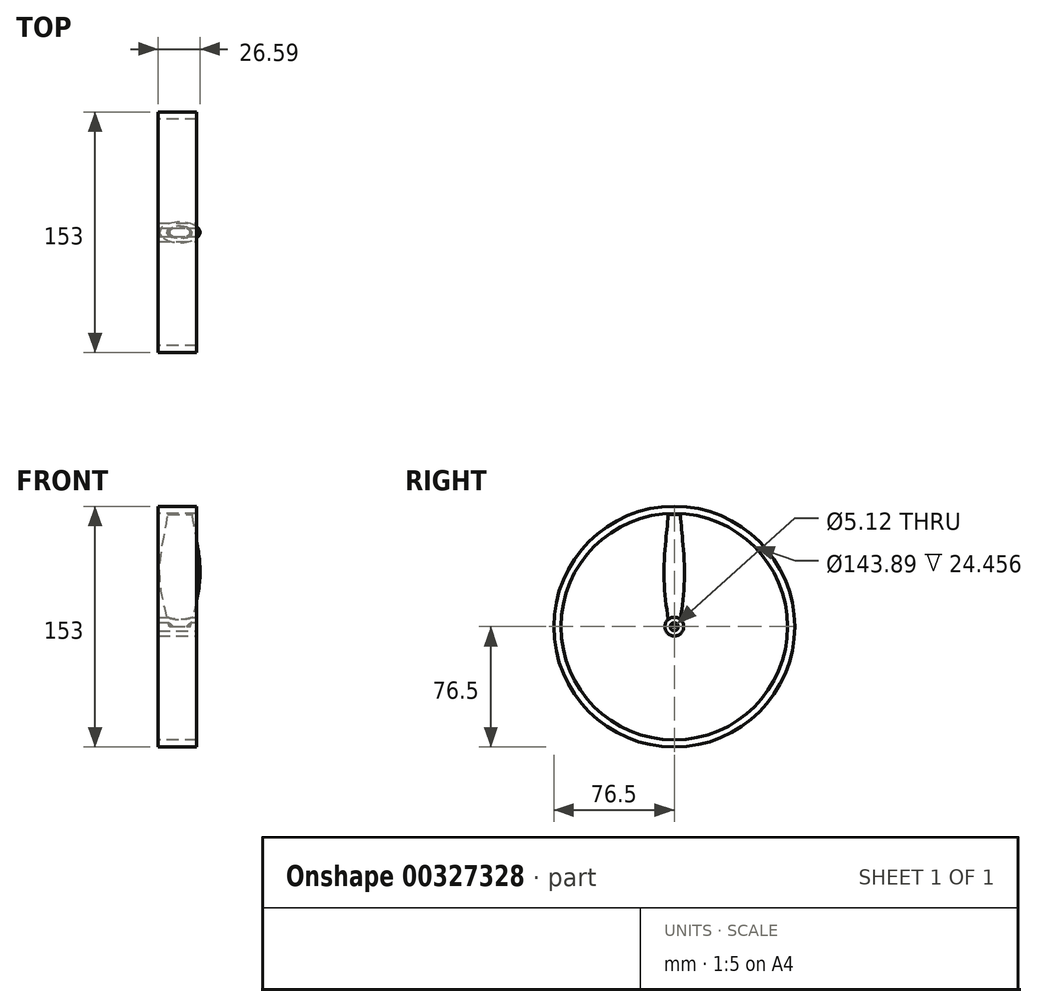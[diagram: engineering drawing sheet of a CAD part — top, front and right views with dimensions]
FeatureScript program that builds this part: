
annotation { "Feature Type Name" : "Feature", "Feature Type Description" : "" }
export const myFeature = defineFeature(function(context is Context, id is Id, definition is map)
    precondition{}
    {
        {
            var Q0;
            Q0=qCreatedBy(makeId("Front.planeOp"),FACE);
            var sketch = newSketch(context, id + "F0", { "sketchPlane" : qUnion([Q0])});
            skLineSegment(sketch, "E0.bottom", {"start": v(-13.8, -76.5) * mm, "end": v(10.66, -76.5) * mm});
            skLineSegment(sketch, "E0.top", {"start": v(-13.8, -71.95) * mm, "end": v(10.66, -71.95) * mm});
            skLineSegment(sketch, "E0.left", {"start": v(-13.8, -76.5) * mm, "end": v(-13.8, -71.95) * mm});
            skLineSegment(sketch, "E0.right", {"start": v(10.66, -76.5) * mm, "end": v(10.66, -71.95) * mm});
            skLineSegment(sketch, "E1", {"start": v(-76.36, 0) * mm, "end": v(77.2, 0) * mm, "construction": true});
            skSolve(sketch);
        }
        {
            var Q0;
            Q0 = qSketchRegion(id + "F0", true);
            var Q1;
            Q1=sQuery(id+"F0.wireOp",EDGE,"E1");
            revolve(context, id + "F1", {"entities" : qUnion([Q0]), "axis" : qUnion([Q1]), "revolveType" : RevolveType.FULL});
        }
        {
            var Q0;
            Q0=qCreatedBy(makeId("Front.planeOp"),FACE);
            var sketch = newSketch(context, id + "F2", { "sketchPlane" : qUnion([Q0])});
            skLineSegment(sketch, "E2.bottom", {"start": v(-13.8, 2.56) * mm, "end": v(10.66, 2.56) * mm});
            skLineSegment(sketch, "E2.top", {"start": v(-13.8, 5.97) * mm, "end": v(10.66, 5.97) * mm});
            skLineSegment(sketch, "E2.left", {"start": v(-13.8, 2.56) * mm, "end": v(-13.8, 5.97) * mm});
            skLineSegment(sketch, "E2.right", {"start": v(10.66, 2.56) * mm, "end": v(10.66, 5.97) * mm});
            skLineSegment(sketch, "E3", {"start": v(-76.36, 0) * mm, "end": v(-68.96, 2.56) * mm, "construction": true});
            skLineSegment(sketch, "E4", {"start": v(76.07, 0) * mm, "end": v(-76.36, 0) * mm, "construction": true});
            skSolve(sketch);
        }
        {
            var Q0;
            Q0=makeQuery(id+"F2.imprint","IMPRINT",FACE,{"disambiguationData":[TD([[makeQuery(id+"F2.imprint","IMPRINT",EDGE,{"derivedFrom":sQuery(id+"F2.wireOp",EDGE,"E2.bottom")}),1.0]])]});
            var Q1;
            Q1=sQuery(id+"F2.wireOp",EDGE,"E4");
            revolve(context, id + "F3", {"entities" : qUnion([Q0]), "axis" : qUnion([Q1]), "revolveType" : RevolveType.FULL});
        }
        {
            var Q0;
            Q0=qCreatedBy(makeId("Top.planeOp"),FACE);
            cPlane(context, id + "F4", {"entities" : qUnion([Q0]), "cplaneType" : CPlaneType.OFFSET, "offset" : 33.02 * mm, "width" : 152.4 * mm, "height" : 152.4 * mm});
        }
        {
            var Q0;
            Q0=qCreatedBy(makeId("Top.planeOp"),FACE);
            var sketch = newSketch(context, id + "F5", { "sketchPlane" : qUnion([Q0])});
            skEllipse(sketch, "E5", {"center": v(0, 0) * mm, "majorRadius": 6.65 * mm, "minorRadius": 3.38 * mm, "majorAxis": v(-1, 0)});
            skSolve(sketch);
        }
        {
            var Q0;
            Q0=qCreatedBy(id+"F4.planeOp",FACE);
            var sketch = newSketch(context, id + "F6", { "sketchPlane" : qUnion([Q0])});
            skEllipse(sketch, "E6", {"center": v(0, 0) * mm, "majorRadius": 12.78 * mm, "minorRadius": 6.5 * mm, "majorAxis": v(-1, 0)});
            skSolve(sketch);
        }
        {
            var Q0;
            Q0=qCreatedBy(id+"F4.planeOp",FACE);
            cPlane(context, id + "F7", {"entities" : qUnion([Q0]), "cplaneType" : CPlaneType.OFFSET, "offset" : 38.1 * mm, "width" : 152.4 * mm, "height" : 152.4 * mm});
        }
        {
            var Q0;
            Q0=qCreatedBy(id+"F7.planeOp",FACE);
            var sketch = newSketch(context, id + "F8", { "sketchPlane" : qUnion([Q0])});
            skEllipse(sketch, "E7", {"center": v(0, 0) * mm, "majorRadius": 7.69 * mm, "minorRadius": 3.91 * mm, "majorAxis": v(-1, 0)});
            skSolve(sketch);
        }
        {
            var Q1;
            Q1 = qSketchRegion(id + "F8", true);
            var Q2;
            Q2 = qSketchRegion(id + "F6", true);
            var Q3;
            Q3 = qSketchRegion(id + "F5", true);
            loft(context, id + "F9", {"operationType" : NewBodyOperationType.ADD, "sheetProfilesArray" : [{ "sheetProfileEntities" : qUnion([Q1]) }, { "sheetProfileEntities" : qUnion([Q2]) }, { "sheetProfileEntities" : qUnion([Q3]) }]});
        }
    });
